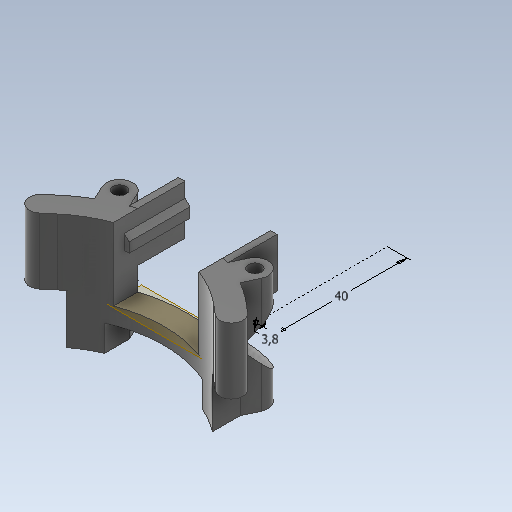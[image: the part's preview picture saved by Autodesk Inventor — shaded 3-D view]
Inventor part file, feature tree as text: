
AUTODESK INVENTOR PART (.ipt)
format: ipt  version: 2020 (Build 240168000, 168)  size: 587,776 bytes
history: native  units: mm
features: sketch x11, extrude x9, projected_geometry x7, other x3, sweep x1
ambient origin geometry x8: Origin, YZ Plane, XZ Plane, XY Plane, X Axis, Y Axis, Z Axis, Center Point
bodies: Body1 (feature_tree)
feature tree (31):
  other  "Твердое тело1"
  extrude  "Выдавливание1"  Depth=35.0mm TaperAngle=0.0deg
  sketch  "Эскиз2"
  extrude  "Выдавливание2"  Depth=4.0mm
  sweep  "Сдвиг1"
  extrude  "Выдавливание5"  Depth=8.0mm
  extrude  "Выдавливание6"  Depth=35.0mm TaperAngle=0.0deg
  extrude  "Выдавливание7"  Depth=8.5mm
  extrude  "Выдавливание8"  TaperAngle=45.0deg  [1 undecoded]
  other  "РабПлоскость1"
  extrude  "Выдавливание9"  Depth=8.5mm
  extrude  "Выдавливание10"  TaperAngle=45.0deg  [1 undecoded]
  extrude  "Выдавливание11"  TaperAngle=0.0deg  [1 undecoded]
  sketch  "Эскиз13"
  other  "РабПлоскость2"
  sketch  "Эскиз1"
  sketch  "Эскиз3"
  projected_geometry  "Спроецированная петля1"
  projected_geometry  "Спроецированная петля2"
  sketch  "3D эскиз1"
  sketch  "Эскиз4"
  sketch  "Эскиз6"
  projected_geometry  "Спроецированная петля4"
  sketch  "Эскиз7"
  projected_geometry  "Спроецированная петля5"
  sketch  "Эскиз9"
  projected_geometry  "Спроецированная петля7"
  sketch  "Эскиз11"
  projected_geometry  "Спроецированная петля8"
  sketch  "Эскиз12"
  projected_geometry  "Спроецированная петля9"
note: 3 required parameter values undecoded (feature->parameter linkage not recoverable at this tier; creation-order binding heuristic only, values carry confidence <= 0.55)
